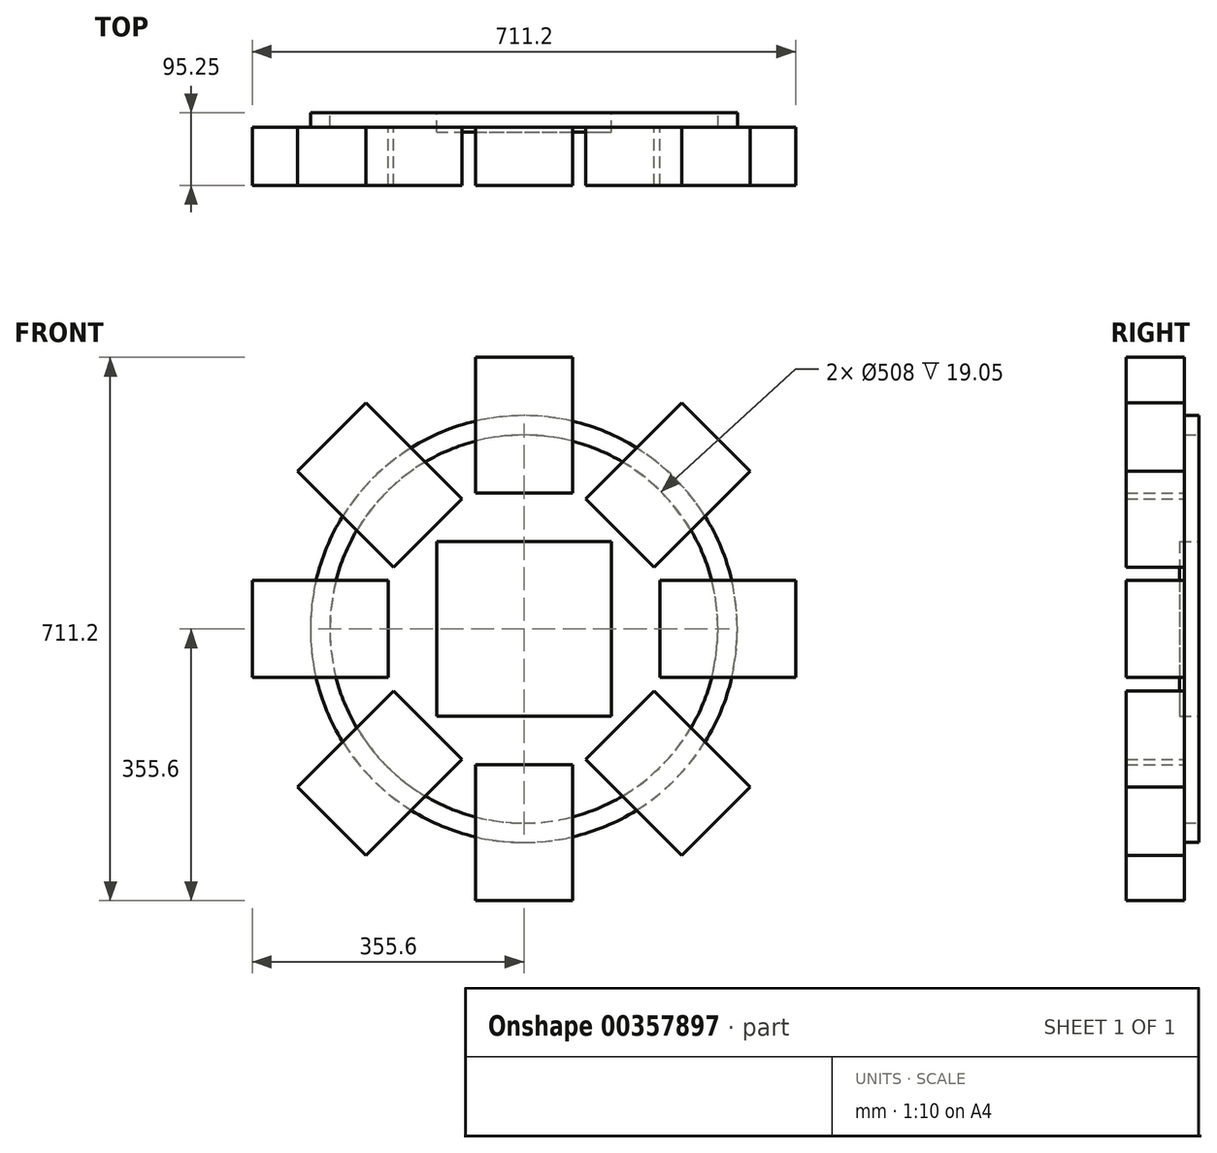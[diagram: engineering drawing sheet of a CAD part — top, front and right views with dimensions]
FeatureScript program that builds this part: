
annotation { "Feature Type Name" : "Feature", "Feature Type Description" : "" }
export const myFeature = defineFeature(function(context is Context, id is Id, definition is map)
    precondition{}
    {
        {
            var Q0;
            Q0=qCreatedBy(makeId("Front.planeOp"),FACE);
            var sketch = newSketch(context, id + "F0", { "sketchPlane" : qUnion([Q0])});
            skCircle(sketch, "E0", {"center": v(0, 0) * mm, "radius": 279.4 * mm});
            skCircle(sketch, "E1", {"center": v(0, 0) * mm, "radius": 254 * mm});
            skSolve(sketch);
        }
        {
            var Q0;
            Q0 = qSketchRegion(id + "F0", true);
            extrude(context, id + "F1", {"entities" : qUnion([Q0]), "depth" : 19.05 * mm});
        }
        {
            var Q0;
            Q0=makeQuery(id+"F1.opExtrude","CAP_FACE",FACE,{"disambiguationData":[OSD([sQuery(id+"F0.wireOp",EDGE,"E0"),sQuery(id+"F0.wireOp",EDGE,"E1")])],"isStart":false});
            var sketch = newSketch(context, id + "F2", { "sketchPlane" : qUnion([Q0])});
            skLineSegment(sketch, "E2.bottom", {"start": v(-63.5, 355.6) * mm, "end": v(63.5, 355.6) * mm});
            skLineSegment(sketch, "E2.top", {"start": v(-63.5, 177.8) * mm, "end": v(63.5, 177.8) * mm});
            skLineSegment(sketch, "E2.left", {"start": v(-63.5, 355.6) * mm, "end": v(-63.5, 177.8) * mm});
            skLineSegment(sketch, "E2.right", {"start": v(63.5, 355.6) * mm, "end": v(63.5, 177.8) * mm});
            skLineSegment(sketch, "E3.1.0", {"start": v(-206.55, 296.35) * mm, "end": v(-80.82, 170.62) * mm});
            skLineSegment(sketch, "E3.1.1", {"start": v(-296.35, 206.55) * mm, "end": v(-170.62, 80.82) * mm});
            skLineSegment(sketch, "E3.1.2", {"start": v(-170.62, 80.82) * mm, "end": v(-80.82, 170.62) * mm});
            skLineSegment(sketch, "E3.1.3", {"start": v(-296.35, 206.55) * mm, "end": v(-206.55, 296.35) * mm});
            skLineSegment(sketch, "E3.2.0", {"start": v(-355.6, 63.5) * mm, "end": v(-177.8, 63.5) * mm});
            skLineSegment(sketch, "E3.2.1", {"start": v(-355.6, -63.5) * mm, "end": v(-177.8, -63.5) * mm});
            skLineSegment(sketch, "E3.2.2", {"start": v(-177.8, -63.5) * mm, "end": v(-177.8, 63.5) * mm});
            skLineSegment(sketch, "E3.2.3", {"start": v(-355.6, -63.5) * mm, "end": v(-355.6, 63.5) * mm});
            skLineSegment(sketch, "E3.3.0", {"start": v(-296.35, -206.55) * mm, "end": v(-170.62, -80.82) * mm});
            skLineSegment(sketch, "E3.3.1", {"start": v(-206.55, -296.35) * mm, "end": v(-80.82, -170.62) * mm});
            skLineSegment(sketch, "E3.3.2", {"start": v(-80.82, -170.62) * mm, "end": v(-170.62, -80.82) * mm});
            skLineSegment(sketch, "E3.3.3", {"start": v(-206.55, -296.35) * mm, "end": v(-296.35, -206.55) * mm});
            skLineSegment(sketch, "E3.4.0", {"start": v(-63.5, -355.6) * mm, "end": v(-63.5, -177.8) * mm});
            skLineSegment(sketch, "E3.4.1", {"start": v(63.5, -355.6) * mm, "end": v(63.5, -177.8) * mm});
            skLineSegment(sketch, "E3.4.2", {"start": v(63.5, -177.8) * mm, "end": v(-63.5, -177.8) * mm});
            skLineSegment(sketch, "E3.4.3", {"start": v(63.5, -355.6) * mm, "end": v(-63.5, -355.6) * mm});
            skLineSegment(sketch, "E3.5.0", {"start": v(206.55, -296.35) * mm, "end": v(80.82, -170.62) * mm});
            skLineSegment(sketch, "E3.5.1", {"start": v(296.35, -206.55) * mm, "end": v(170.62, -80.82) * mm});
            skLineSegment(sketch, "E3.5.2", {"start": v(170.62, -80.82) * mm, "end": v(80.82, -170.62) * mm});
            skLineSegment(sketch, "E3.5.3", {"start": v(296.35, -206.55) * mm, "end": v(206.55, -296.35) * mm});
            skLineSegment(sketch, "E3.6.0", {"start": v(355.6, -63.5) * mm, "end": v(177.8, -63.5) * mm});
            skLineSegment(sketch, "E3.6.1", {"start": v(355.6, 63.5) * mm, "end": v(177.8, 63.5) * mm});
            skLineSegment(sketch, "E3.6.2", {"start": v(177.8, 63.5) * mm, "end": v(177.8, -63.5) * mm});
            skLineSegment(sketch, "E3.6.3", {"start": v(355.6, 63.5) * mm, "end": v(355.6, -63.5) * mm});
            skLineSegment(sketch, "E3.7.0", {"start": v(296.35, 206.55) * mm, "end": v(170.62, 80.82) * mm});
            skLineSegment(sketch, "E3.7.1", {"start": v(206.55, 296.35) * mm, "end": v(80.82, 170.62) * mm});
            skLineSegment(sketch, "E3.7.2", {"start": v(80.82, 170.62) * mm, "end": v(170.62, 80.82) * mm});
            skLineSegment(sketch, "E3.7.3", {"start": v(206.55, 296.35) * mm, "end": v(296.35, 206.55) * mm});
            skPoint(sketch, "E3.center", {"position": v(0, 0) * mm});
            skSolve(sketch);
        }
        {
            var Q0;
            {var subQ0=sQuery(id+"F2.wireOp",EDGE,"E2.left");var subQ1=makeQuery(id+"F1.opExtrude","CAP_EDGE",EDGE,{"disambiguationData":[OSD([sQuery(id+"F0.wireOp",EDGE,"E0")])],"isStart":false});var subQ2=makeQuery(id+"F2.imprint","INTERSECT",VERTEX,{"derivedFrom":[subQ1,subQ0]});Q0=makeQuery(id+"F2.imprint","IMPRINT",FACE,{"disambiguationData":[TD([[makeQuery(id+"F2.imprint","IMPRINT",EDGE,{"disambiguationData":[TD([[subQ2,-1.0]])],"derivedFrom":subQ0}),1.0]])]});}
            var Q1;
            {var subQ0=sQuery(id+"F2.wireOp",EDGE,"E2.top");Q1=makeQuery(id+"F2.imprint","IMPRINT",FACE,{"disambiguationData":[TD([[makeQuery(id+"F2.imprint","IMPRINT",EDGE,{"derivedFrom":subQ0}),1.0]])]});}
            var Q2;
            {var subQ0=sQuery(id+"F2.wireOp",EDGE,"E2.bottom");Q2=makeQuery(id+"F2.imprint","IMPRINT",FACE,{"disambiguationData":[TD([[makeQuery(id+"F2.imprint","IMPRINT",EDGE,{"derivedFrom":subQ0}),-1.0]])]});}
            extrude(context, id + "F3", {"entities" : qUnion([Q0, Q1, Q2]), "depth" : 76.2 * mm});
        }
        {
            var Q0;
            Q0 = qSketchRegion(id + "F2", true);
            extrude(context, id + "F4", {"entities" : qUnion([Q0]), "depth" : 76.2 * mm});
        }
        {
            var Q0;
            Q0=qCreatedBy(makeId("Front.planeOp"),FACE);
            var sketch = newSketch(context, id + "F5", { "sketchPlane" : qUnion([Q0])});
            skLineSegment(sketch, "E4.bottom", {"start": v(-114.3, 114.3) * mm, "end": v(114.3, 114.3) * mm});
            skLineSegment(sketch, "E4.top", {"start": v(-114.3, -114.3) * mm, "end": v(114.3, -114.3) * mm});
            skLineSegment(sketch, "E4.left", {"start": v(-114.3, 114.3) * mm, "end": v(-114.3, -114.3) * mm});
            skLineSegment(sketch, "E4.right", {"start": v(114.3, 114.3) * mm, "end": v(114.3, -114.3) * mm});
            skSolve(sketch);
        }
        {
            var Q0;
            Q0=makeQuery(id+"F5.imprint","IMPRINT",FACE,{"disambiguationData":[TD([[makeQuery(id+"F5.imprint","IMPRINT",EDGE,{"derivedFrom":sQuery(id+"F5.wireOp",EDGE,"E4.bottom")}),-1.0]])]});
            extrude(context, id + "F6", {"entities" : qUnion([Q0]), "depth" : 25.4 * mm});
        }
    });
